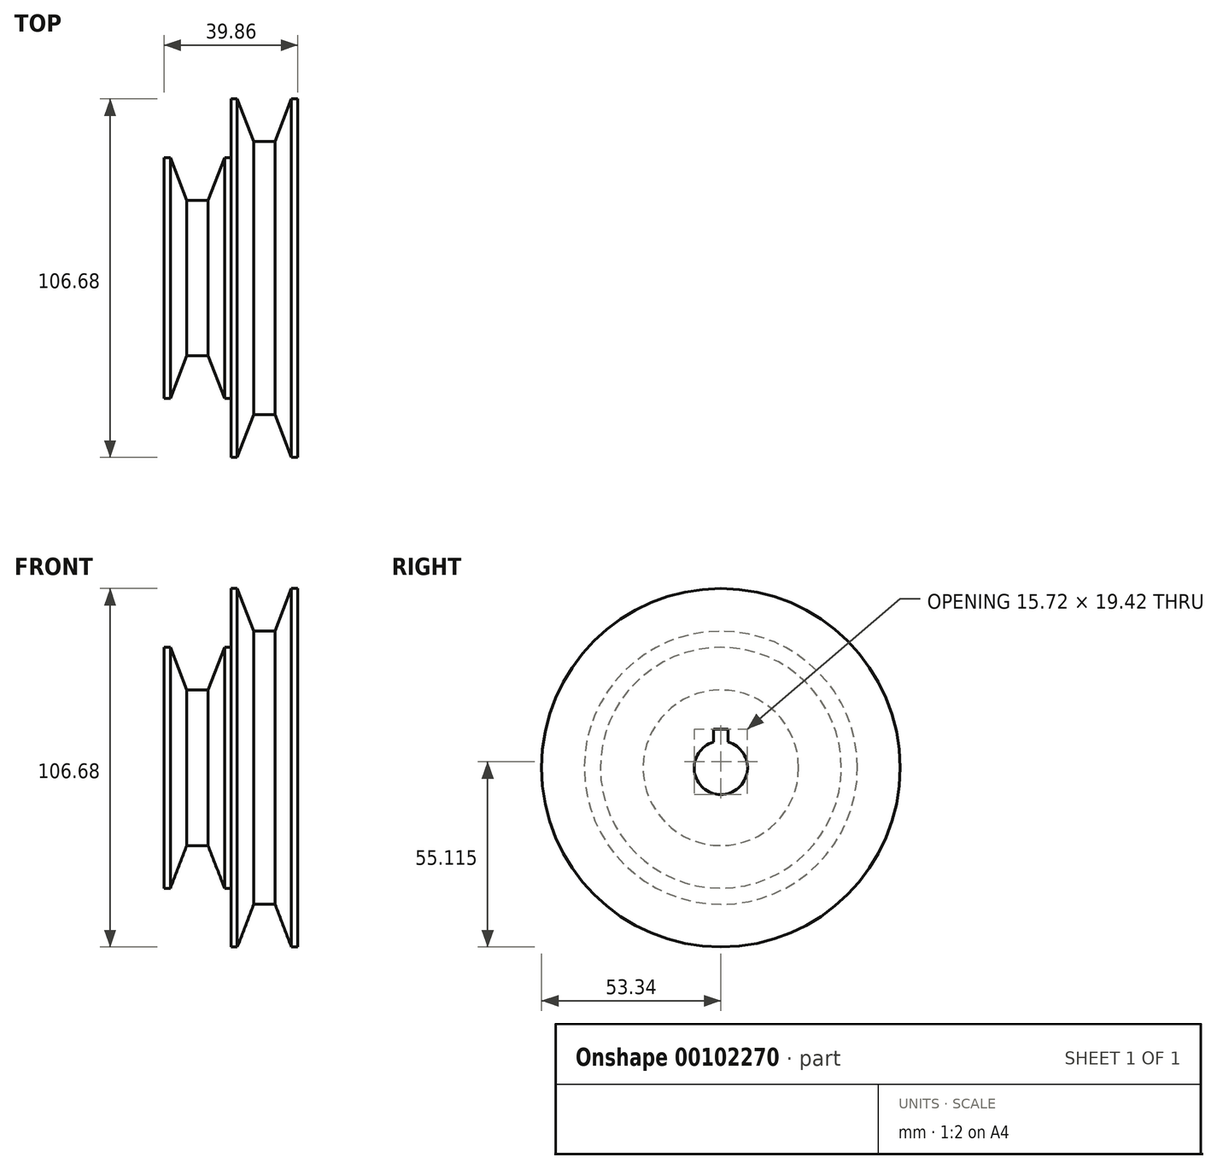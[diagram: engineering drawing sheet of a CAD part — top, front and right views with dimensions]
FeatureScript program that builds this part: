
annotation { "Feature Type Name" : "Feature", "Feature Type Description" : "" }
export const myFeature = defineFeature(function(context is Context, id is Id, definition is map)
    precondition{}
    {
        {
            var Q0;
            Q0=qCreatedBy(makeId("Front.planeOp"),FACE);
            var sketch = newSketch(context, id + "F0", { "sketchPlane" : qUnion([Q0])});
            skLineSegment(sketch, "E0", {"start": v(0, 0) * mm, "end": v(-180.2, 0) * mm, "construction": true});
            skLineSegment(sketch, "E1", {"start": v(0, 0) * mm, "end": v(273.2, 0) * mm, "construction": true});
            skLineSegment(sketch, "E2", {"start": v(0, 0) * mm, "end": v(0, 113.9) * mm, "construction": true});
            skLineSegment(sketch, "E3", {"start": v(-19.93, 7.94) * mm, "end": v(19.93, 7.94) * mm});
            skLineSegment(sketch, "E4", {"start": v(0, 7.94) * mm, "end": v(0, 35.84) * mm});
            skLineSegment(sketch, "E5", {"start": v(0, 35.84) * mm, "end": v(-1.9, 35.84) * mm});
            skLineSegment(sketch, "E6", {"start": v(-1.9, 35.84) * mm, "end": v(-6.79, 23.14) * mm});
            skLineSegment(sketch, "E7", {"start": v(-6.79, 23.14) * mm, "end": v(-9.96, 23.14) * mm});
            skLineSegment(sketch, "E8.MirrorCS", {"start": v(-19.93, 7.94) * mm, "end": v(-19.93, 35.84) * mm});
            skLineSegment(sketch, "E9.MirrorCS", {"start": v(-18.03, 35.84) * mm, "end": v(-13.14, 23.14) * mm});
            skLineSegment(sketch, "E10.MirrorCS", {"start": v(-13.14, 23.14) * mm, "end": v(-9.96, 23.14) * mm});
            skLineSegment(sketch, "E11", {"start": v(0, 35.84) * mm, "end": v(0, 53.34) * mm});
            skLineSegment(sketch, "E12", {"start": v(0, 53.34) * mm, "end": v(1.9, 53.34) * mm});
            skLineSegment(sketch, "E13", {"start": v(1.9, 53.34) * mm, "end": v(6.79, 40.64) * mm});
            skLineSegment(sketch, "E14", {"start": v(6.79, 40.64) * mm, "end": v(9.96, 40.64) * mm});
            skLineSegment(sketch, "E15.MirrorCS", {"start": v(13.14, 40.64) * mm, "end": v(9.96, 40.64) * mm});
            skLineSegment(sketch, "E16.MirrorCS", {"start": v(18.03, 53.34) * mm, "end": v(13.14, 40.64) * mm});
            skLineSegment(sketch, "E17.MirrorCS", {"start": v(19.93, 53.34) * mm, "end": v(18.03, 53.34) * mm});
            skLineSegment(sketch, "E18.MirrorCS", {"start": v(19.93, 35.84) * mm, "end": v(19.93, 53.34) * mm});
            skLineSegment(sketch, "E19.MirrorCS", {"start": v(19.93, 7.94) * mm, "end": v(19.93, 35.84) * mm});
            skLineSegment(sketch, "E20.MirrorCS", {"start": v(0, -35.84) * mm, "end": v(-1.9, -35.84) * mm});
            skLineSegment(sketch, "E21.MirrorCS", {"start": v(13.14, -40.64) * mm, "end": v(9.96, -40.64) * mm});
            skLineSegment(sketch, "E22.MirrorCS", {"start": v(19.93, -53.34) * mm, "end": v(18.03, -53.34) * mm});
            skLineSegment(sketch, "E23.MirrorCS", {"start": v(-19.93, -35.84) * mm, "end": v(-18.03, -35.84) * mm});
            skLineSegment(sketch, "E24.MirrorCS", {"start": v(-6.79, -23.14) * mm, "end": v(-9.96, -23.14) * mm});
            skLineSegment(sketch, "E25.MirrorCS", {"start": v(0, -53.34) * mm, "end": v(1.9, -53.34) * mm});
            skLineSegment(sketch, "E26.MirrorCS", {"start": v(6.79, -40.64) * mm, "end": v(9.96, -40.64) * mm});
            skLineSegment(sketch, "E27.MirrorCS", {"start": v(-13.14, -23.14) * mm, "end": v(-9.96, -23.14) * mm});
            skLineSegment(sketch, "E28.MirrorCS", {"start": v(19.93, -35.84) * mm, "end": v(19.93, -53.34) * mm});
            skLineSegment(sketch, "E29.MirrorCS", {"start": v(-1.9, -35.84) * mm, "end": v(-6.79, -23.14) * mm});
            skLineSegment(sketch, "E30.MirrorCS", {"start": v(-19.93, -7.94) * mm, "end": v(-19.93, -35.84) * mm});
            skLineSegment(sketch, "E31.MirrorCS", {"start": v(0, -7.94) * mm, "end": v(0, -35.84) * mm});
            skLineSegment(sketch, "E32.MirrorCS", {"start": v(-19.93, -7.94) * mm, "end": v(19.93, -7.94) * mm});
            skLineSegment(sketch, "E33.MirrorCS", {"start": v(0, -35.84) * mm, "end": v(0, -53.34) * mm});
            skLineSegment(sketch, "E34.MirrorCS", {"start": v(19.93, -7.94) * mm, "end": v(19.93, -35.84) * mm});
            skLineSegment(sketch, "E35.MirrorCS", {"start": v(1.9, -53.34) * mm, "end": v(6.79, -40.64) * mm});
            skLineSegment(sketch, "E36.MirrorCS", {"start": v(-18.03, -35.84) * mm, "end": v(-13.14, -23.14) * mm});
            skLineSegment(sketch, "E37.MirrorCS", {"start": v(18.03, -53.34) * mm, "end": v(13.14, -40.64) * mm});
            skPoint(sketch, "E38.orphan", {"position": v(-59.91, 7.94) * mm});
            skPoint(sketch, "E39.orphan", {"position": v(97.36, 7.94) * mm});
            skPoint(sketch, "E40.orphan", {"position": v(97.36, -7.94) * mm});
            skPoint(sketch, "E41.orphan", {"position": v(-59.91, -7.94) * mm});
            skLineSegment(sketch, "E42", {"start": v(-18.03, 35.84) * mm, "end": v(-19.93, 35.84) * mm});
            skSolve(sketch);
        }
        {
            var Q0;
            {var subQ2=sQuery(id+"F0.wireOp",EDGE,"E4");Q0=makeQuery(id+"F0.imprint","IMPRINT",FACE,{"disambiguationData":[TD([[makeQuery(id+"F0.imprint","IMPRINT",EDGE,{"derivedFrom":subQ2}),-1.0]])]});}
            var Q1;
            {var subQ0=sQuery(id+"F0.wireOp",EDGE,"E4");Q1=makeQuery(id+"F0.imprint","IMPRINT",FACE,{"disambiguationData":[TD([[makeQuery(id+"F0.imprint","IMPRINT",EDGE,{"derivedFrom":subQ0}),1.0]])]});}
            var Q2;
            Q2=makeQuery(id+"F0.imprint","IMPRINT",FACE,{"disambiguationData":[TD([[makeQuery(id+"F0.imprint","IMPRINT",EDGE,{"derivedFrom":sQuery(id+"F0.wireOp",EDGE,"E20.MirrorCS")}),-1.0]])]});
            var Q3;
            Q3=makeQuery(id+"F0.imprint","IMPRINT",FACE,{"disambiguationData":[TD([[makeQuery(id+"F0.imprint","IMPRINT",EDGE,{"derivedFrom":sQuery(id+"F0.wireOp",EDGE,"E21.MirrorCS")}),-1.0]])]});
            var Q4;
            Q4=sQuery(id+"F0.wireOp",EDGE,"E0");
            revolve(context, id + "F1", {"entities" : qUnion([Q0, Q1, Q2, Q3]), "axis" : qUnion([Q4]), "revolveType" : RevolveType.FULL});
        }
        {
            var Q0;
            Q0=qCreatedBy(makeId("Right.planeOp"),FACE);
            var sketch = newSketch(context, id + "F2", { "sketchPlane" : qUnion([Q0])});
            skLineSegment(sketch, "E43.top", {"start": v(2.18, 11.49) * mm, "end": v(-2.18, 11.49) * mm});
            skLineSegment(sketch, "E43.left", {"start": v(2.18, 0) * mm, "end": v(2.18, 11.49) * mm});
            skLineSegment(sketch, "E43.right", {"start": v(-2.18, 0) * mm, "end": v(-2.18, 11.49) * mm});
            skPoint(sketch, "E43.middle", {"position": v(0, 0) * mm});
            skLineSegment(sketch, "E44", {"start": v(0, 0) * mm, "end": v(2.18, 0) * mm});
            skPoint(sketch, "E44.endSnap0", {"position": v(2.18, 0) * mm});
            skLineSegment(sketch, "E45", {"start": v(2.18, 0) * mm, "end": v(-2.18, 0) * mm});
            skPoint(sketch, "E43.bottom.end.orphan", {"position": v(-2.18, -11.49) * mm});
            skPoint(sketch, "E43.bottom.start.orphan", {"position": v(2.18, -11.49) * mm});
            skPoint(sketch, "E46.orphan", {"position": v(11.88, 0) * mm});
            skSolve(sketch);
        }
        {
            var Q0;
            Q0=makeQuery(id+"F2.imprint","IMPRINT",FACE,{"disambiguationData":[TD([[makeQuery(id+"F2.imprint","IMPRINT",EDGE,{"derivedFrom":sQuery(id+"F2.wireOp",EDGE,"E43.top")}),1.0]])]});
            extrude(context, id + "F3", {"entities" : qUnion([Q0]), "operationType" : NewBodyOperationType.REMOVE, "endBound" : BoundingType.SYMMETRIC, "depth" : 101.6 * mm});
        }
        {
            var Q0;
            Q0=makeQuery(id+"F1.opRevolve","SWEPT_BODY",BODY,{"disambiguationData":[OSD([sQuery(id+"F0.wireOp",EDGE,"E20.MirrorCS"),sQuery(id+"F0.wireOp",EDGE,"E21.MirrorCS"),sQuery(id+"F0.wireOp",EDGE,"E22.MirrorCS"),sQuery(id+"F0.wireOp",EDGE,"E23.MirrorCS"),sQuery(id+"F0.wireOp",EDGE,"E24.MirrorCS"),sQuery(id+"F0.wireOp",EDGE,"E25.MirrorCS"),sQuery(id+"F0.wireOp",EDGE,"E26.MirrorCS"),sQuery(id+"F0.wireOp",EDGE,"E27.MirrorCS"),sQuery(id+"F0.wireOp",EDGE,"E28.MirrorCS"),sQuery(id+"F0.wireOp",EDGE,"E29.MirrorCS"),sQuery(id+"F0.wireOp",EDGE,"E30.MirrorCS"),sQuery(id+"F0.wireOp",EDGE,"E32.MirrorCS"),sQuery(id+"F0.wireOp",EDGE,"E33.MirrorCS"),sQuery(id+"F0.wireOp",EDGE,"E34.MirrorCS"),sQuery(id+"F0.wireOp",EDGE,"E35.MirrorCS"),sQuery(id+"F0.wireOp",EDGE,"E36.MirrorCS"),sQuery(id+"F0.wireOp",EDGE,"E37.MirrorCS")])]});
            deleteBodies(context, id + "F4", {"entities" : qUnion([Q0])});
        }
    });
